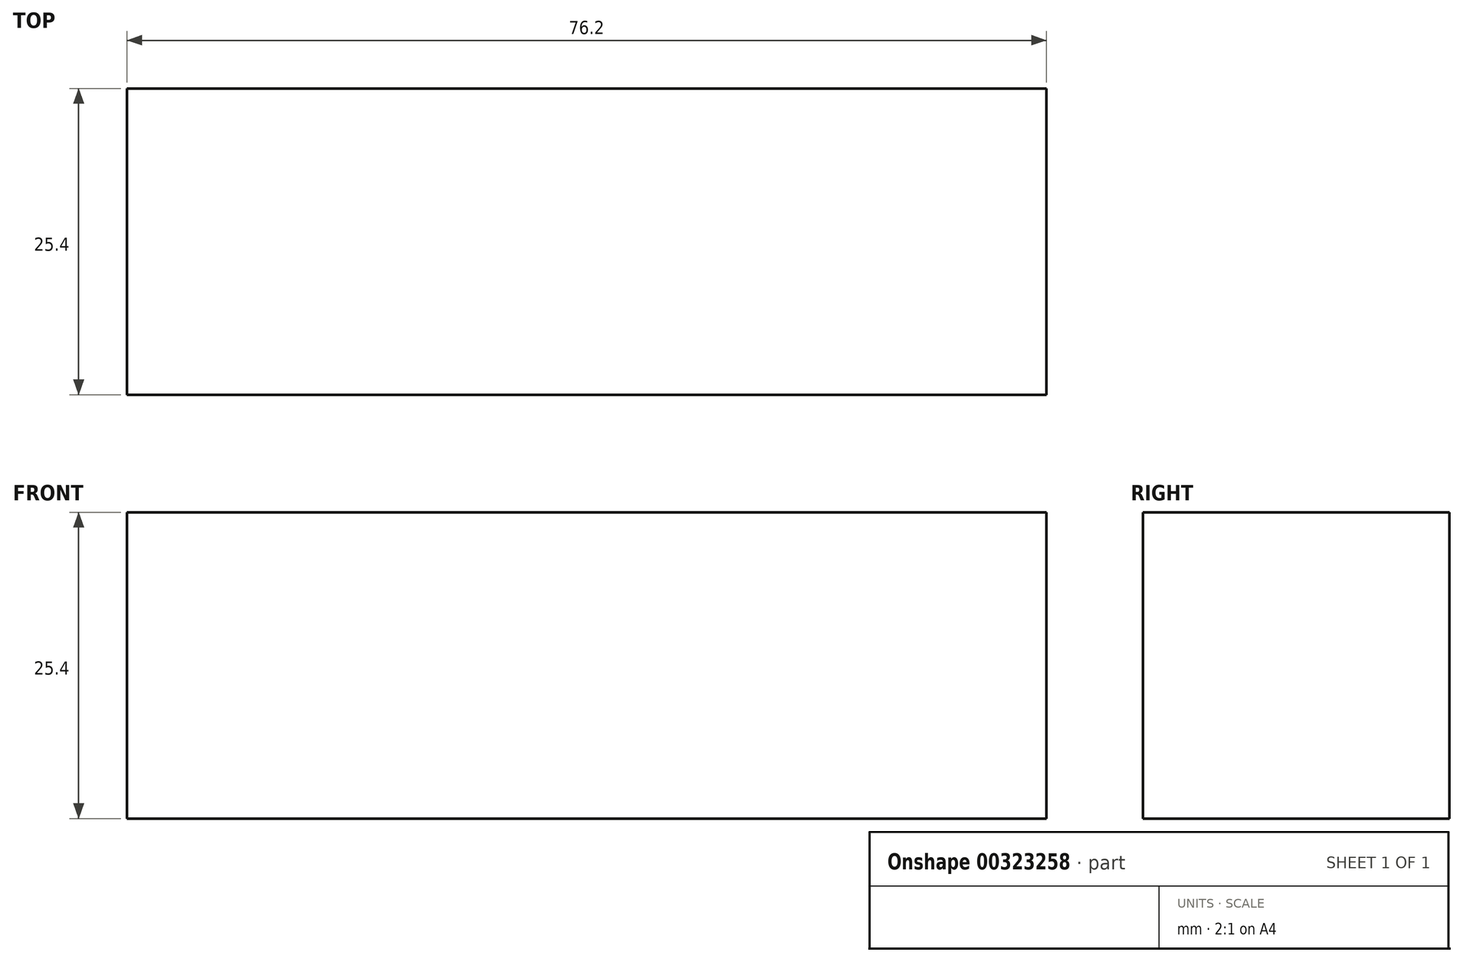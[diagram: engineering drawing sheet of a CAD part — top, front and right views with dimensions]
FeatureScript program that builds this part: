
annotation { "Feature Type Name" : "Feature", "Feature Type Description" : "" }
export const myFeature = defineFeature(function(context is Context, id is Id, definition is map)
    precondition{}
    {
        {
            var Q0;
            Q0=qCreatedBy(makeId("Right.planeOp"),FACE);
            var sketch = newSketch(context, id + "F0", { "sketchPlane" : qUnion([Q0])});
            skLineSegment(sketch, "E0.bottom", {"start": v(12.7, 12.7) * mm, "end": v(-12.7, 12.7) * mm});
            skLineSegment(sketch, "E0.top", {"start": v(12.7, -12.7) * mm, "end": v(-12.7, -12.7) * mm});
            skLineSegment(sketch, "E0.left", {"start": v(12.7, 12.7) * mm, "end": v(12.7, -12.7) * mm});
            skLineSegment(sketch, "E0.right", {"start": v(-12.7, 12.7) * mm, "end": v(-12.7, -12.7) * mm});
            skPoint(sketch, "E0.middle", {"position": v(0, 0) * mm});
            skSolve(sketch);
        }
        {
            var Q0;
            Q0 = qSketchRegion(id + "F0", true);
            extrude(context, id + "F1", {"entities" : qUnion([Q0]), "endBound" : BoundingType.SYMMETRIC, "depth" : 76.2 * mm});
        }
    });
